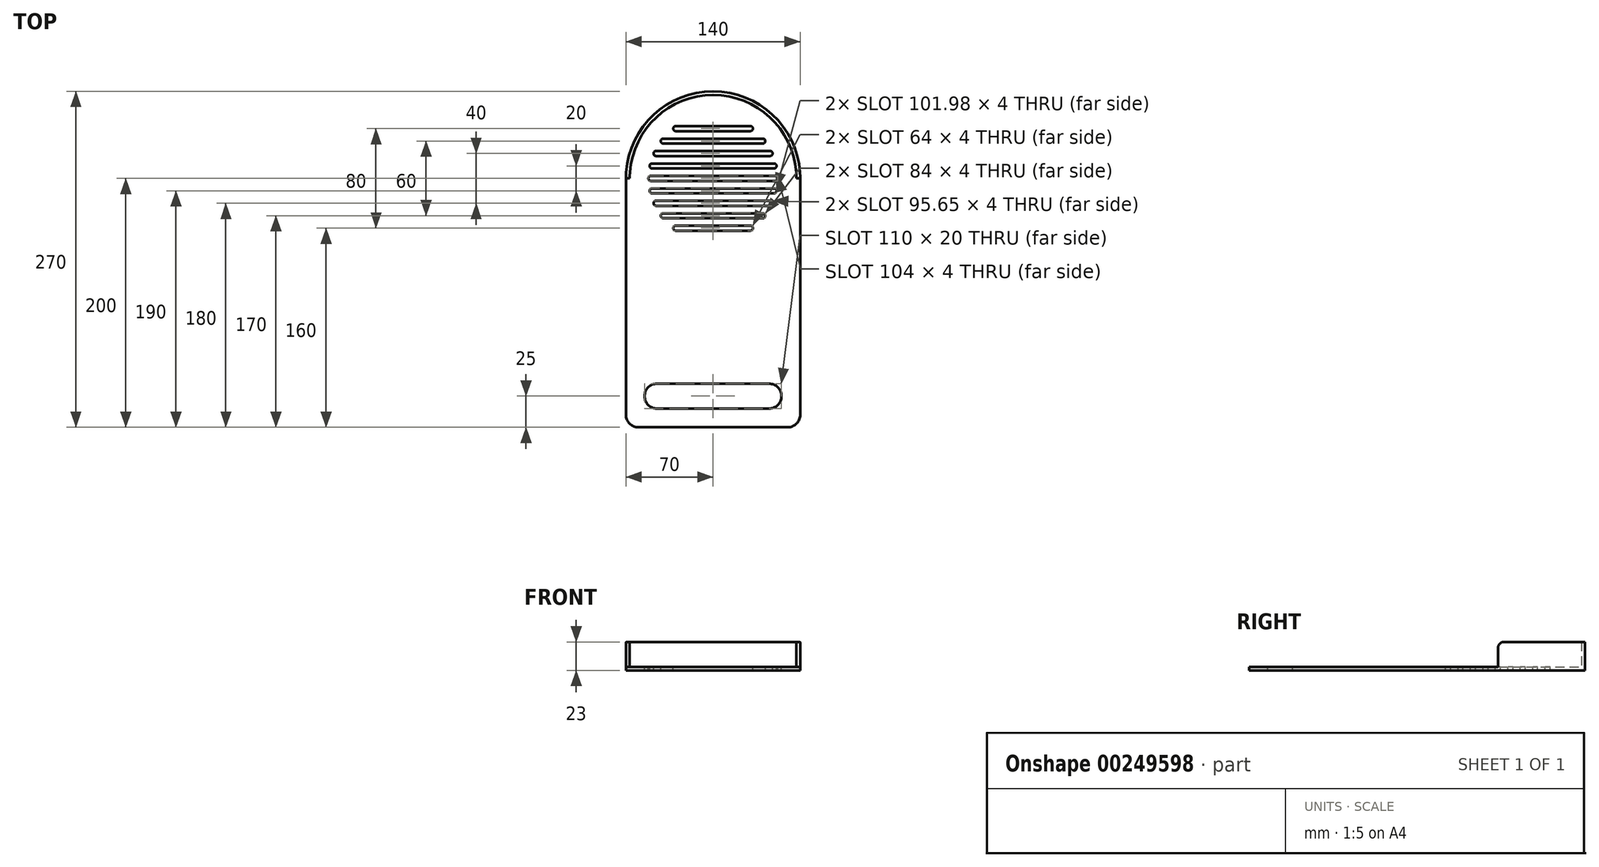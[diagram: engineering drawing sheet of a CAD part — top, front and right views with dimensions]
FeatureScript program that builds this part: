
annotation { "Feature Type Name" : "Feature", "Feature Type Description" : "" }
export const myFeature = defineFeature(function(context is Context, id is Id, definition is map)
    precondition{}
    {
        {
            var Q0;
            Q0=qCreatedBy(makeId("Top.planeOp"),FACE);
            var sketch = newSketch(context, id + "F0", { "sketchPlane" : qUnion([Q0])});
            skArc(sketch, "E0", {"start": v(70, 0) * mm, "mid": v(0, 70) * mm, "end": v(-70, 0) * mm});
            skLineSegment(sketch, "E1.top", {"start": v(-60, -200) * mm, "end": v(60, -200) * mm});
            skLineSegment(sketch, "E1.left", {"start": v(-70, 0) * mm, "end": v(-70, -190) * mm});
            skLineSegment(sketch, "E1.right", {"start": v(70, 0) * mm, "end": v(70, -190) * mm});
            skPoint(sketch, "E2.visualSharp", {"position": v(-70, -200) * mm});
            skArc(sketch, "E2.filletArc", {"start": v(-70, -190) * mm, "mid": v(-67.07, -197.07) * mm, "end": v(-60, -200) * mm});
            skPoint(sketch, "E3.visualSharp", {"position": v(70, -200) * mm});
            skArc(sketch, "E3.filletArc", {"start": v(60, -200) * mm, "mid": v(67.07, -197.07) * mm, "end": v(70, -190) * mm});
            skArc(sketch, "E4.0", {"start": v(67, 0) * mm, "mid": v(0, 67) * mm, "end": v(-67, 0) * mm});
            skLineSegment(sketch, "E5", {"start": v(-67, 0) * mm, "end": v(-70, 0) * mm});
            skLineSegment(sketch, "E6", {"start": v(67, 0) * mm, "end": v(70, 0) * mm});
            skLineSegment(sketch, "E7", {"start": v(-50, 0) * mm, "end": v(50, 0) * mm});
            skLineSegment(sketch, "E8", {"start": v(-48.99, 10) * mm, "end": v(48.99, 10) * mm});
            skLineSegment(sketch, "E9", {"start": v(-45.83, 20) * mm, "end": v(45.83, 20) * mm});
            skLineSegment(sketch, "E10", {"start": v(-40, 30) * mm, "end": v(40, 30) * mm});
            skLineSegment(sketch, "E11", {"start": v(-30, 40) * mm, "end": v(30, 40) * mm});
            skArc(sketch, "E12.0", {"start": v(50, 0) * mm, "mid": v(0, 50) * mm, "end": v(-50, 0) * mm, "construction": true});
            skArc(sketch, "E13.0.startCap", {"start": v(-50, -2) * mm, "mid": v(-52, 0) * mm, "end": v(-50, 2) * mm});
            skArc(sketch, "E13.0.endCap", {"start": v(50, 2) * mm, "mid": v(52, 0) * mm, "end": v(50, -2) * mm});
            skLineSegment(sketch, "E13.0.left", {"start": v(-50, 2) * mm, "end": v(50, 2) * mm});
            skLineSegment(sketch, "E13.0.right", {"start": v(-50, -2) * mm, "end": v(50, -2) * mm});
            skArc(sketch, "E14.0.startCap", {"start": v(-48.99, 8) * mm, "mid": v(-50.99, 10) * mm, "end": v(-48.99, 12) * mm});
            skArc(sketch, "E14.0.endCap", {"start": v(48.99, 12) * mm, "mid": v(50.99, 10) * mm, "end": v(48.99, 8) * mm});
            skLineSegment(sketch, "E14.0.left", {"start": v(-48.99, 12) * mm, "end": v(48.99, 12) * mm});
            skLineSegment(sketch, "E14.0.right", {"start": v(-48.99, 8) * mm, "end": v(48.99, 8) * mm});
            skArc(sketch, "E14.1.startCap", {"start": v(-45.83, 18) * mm, "mid": v(-47.83, 20) * mm, "end": v(-45.83, 22) * mm});
            skArc(sketch, "E14.1.endCap", {"start": v(45.83, 22) * mm, "mid": v(47.83, 20) * mm, "end": v(45.83, 18) * mm});
            skLineSegment(sketch, "E14.1.left", {"start": v(-45.83, 22) * mm, "end": v(45.83, 22) * mm});
            skLineSegment(sketch, "E14.1.right", {"start": v(-45.83, 18) * mm, "end": v(45.83, 18) * mm});
            skArc(sketch, "E14.2.startCap", {"start": v(-40, 28) * mm, "mid": v(-42, 30) * mm, "end": v(-40, 32) * mm});
            skArc(sketch, "E14.2.endCap", {"start": v(40, 32) * mm, "mid": v(42, 30) * mm, "end": v(40, 28) * mm});
            skLineSegment(sketch, "E14.2.left", {"start": v(-40, 32) * mm, "end": v(40, 32) * mm});
            skLineSegment(sketch, "E14.2.right", {"start": v(-40, 28) * mm, "end": v(40, 28) * mm});
            skArc(sketch, "E14.3.startCap", {"start": v(-30, 38) * mm, "mid": v(-32, 40) * mm, "end": v(-30, 42) * mm});
            skArc(sketch, "E14.3.endCap", {"start": v(30, 42) * mm, "mid": v(32, 40) * mm, "end": v(30, 38) * mm});
            skLineSegment(sketch, "E14.3.left", {"start": v(-30, 42) * mm, "end": v(30, 42) * mm});
            skLineSegment(sketch, "E14.3.right", {"start": v(-30, 38) * mm, "end": v(30, 38) * mm});
            skArc(sketch, "E15.MirrorCS", {"start": v(-48.99, -8) * mm, "mid": v(-50.99, -10) * mm, "end": v(-48.99, -12) * mm});
            skLineSegment(sketch, "E16.MirrorCS", {"start": v(-48.99, -12) * mm, "end": v(48.99, -12) * mm});
            skLineSegment(sketch, "E17.MirrorCS", {"start": v(-48.99, -8) * mm, "end": v(48.99, -8) * mm});
            skArc(sketch, "E18.MirrorCS", {"start": v(48.99, -12) * mm, "mid": v(50.99, -10) * mm, "end": v(48.99, -8) * mm});
            skArc(sketch, "E19.MirrorCS", {"start": v(30, -42) * mm, "mid": v(32, -40) * mm, "end": v(30, -38) * mm});
            skLineSegment(sketch, "E20.MirrorCS", {"start": v(-30, -42) * mm, "end": v(30, -42) * mm});
            skLineSegment(sketch, "E21.MirrorCS", {"start": v(-30, -38) * mm, "end": v(30, -38) * mm});
            skArc(sketch, "E22.MirrorCS", {"start": v(-30, -38) * mm, "mid": v(-32, -40) * mm, "end": v(-30, -42) * mm});
            skArc(sketch, "E23.MirrorCS", {"start": v(-40, -28) * mm, "mid": v(-42, -30) * mm, "end": v(-40, -32) * mm});
            skLineSegment(sketch, "E24.MirrorCS", {"start": v(-40, -32) * mm, "end": v(40, -32) * mm});
            skLineSegment(sketch, "E25.MirrorCS", {"start": v(-40, -28) * mm, "end": v(40, -28) * mm});
            skArc(sketch, "E26.MirrorCS", {"start": v(40, -32) * mm, "mid": v(42, -30) * mm, "end": v(40, -28) * mm});
            skArc(sketch, "E27.MirrorCS", {"start": v(45.83, -22) * mm, "mid": v(47.83, -20) * mm, "end": v(45.83, -18) * mm});
            skLineSegment(sketch, "E28.MirrorCS", {"start": v(-45.83, -22) * mm, "end": v(45.83, -22) * mm});
            skLineSegment(sketch, "E29.MirrorCS", {"start": v(-45.83, -18) * mm, "end": v(45.83, -18) * mm});
            skArc(sketch, "E30.MirrorCS", {"start": v(-45.83, -18) * mm, "mid": v(-47.83, -20) * mm, "end": v(-45.83, -22) * mm});
            skLineSegment(sketch, "E31", {"start": v(-45, -175) * mm, "end": v(45, -175) * mm});
            skLineSegment(sketch, "E32", {"start": v(0, -70) * mm, "end": v(0, -200) * mm, "construction": true});
            skPoint(sketch, "E33", {"position": v(0, -175) * mm});
            skArc(sketch, "E34.0.startCap", {"start": v(-45, -185) * mm, "mid": v(-55, -175) * mm, "end": v(-45, -165) * mm});
            skArc(sketch, "E34.0.endCap", {"start": v(45, -165) * mm, "mid": v(55, -175) * mm, "end": v(45, -185) * mm});
            skLineSegment(sketch, "E34.0.left", {"start": v(-45, -165) * mm, "end": v(45, -165) * mm});
            skLineSegment(sketch, "E34.0.right", {"start": v(-45, -185) * mm, "end": v(45, -185) * mm});
            skSolve(sketch);
        }
        {
            var Q0;
            Q0=makeQuery(id+"F0.imprint","IMPRINT",FACE,{"disambiguationData":[TD([[makeQuery(id+"F0.imprint","IMPRINT",EDGE,{"derivedFrom":sQuery(id+"F0.wireOp",EDGE,"E1.top")}),1.0]])]});
            var Q1;
            Q1=makeQuery(id+"F0.imprint","IMPRINT",FACE,{"disambiguationData":[TD([[makeQuery(id+"F0.imprint","IMPRINT",EDGE,{"derivedFrom":sQuery(id+"F0.wireOp",EDGE,"E0")}),1.0]])]});
            extrude(context, id + "F1", {"entities" : qUnion([Q0, Q1]), "oppositeDirection" : true, "depth" : 3 * mm});
        }
        {
            var Q0;
            Q0=makeQuery(id+"F0.imprint","IMPRINT",FACE,{"disambiguationData":[TD([[makeQuery(id+"F0.imprint","IMPRINT",EDGE,{"derivedFrom":sQuery(id+"F0.wireOp",EDGE,"E0")}),1.0]])]});
            extrude(context, id + "F2", {"entities" : qUnion([Q0]), "operationType" : NewBodyOperationType.ADD, "depth" : 20 * mm});
        }
        {
            var Q0;
            Q0=makeQuery(id+"F2.opExtrude","CAP_EDGE",EDGE,{"disambiguationData":[OSD([sQuery(id+"F0.wireOp",EDGE,"E5")])],"isStart":false});
            var Q1;
            Q1=makeQuery(id+"F2.opExtrude","CAP_EDGE",EDGE,{"disambiguationData":[OSD([sQuery(id+"F0.wireOp",EDGE,"E6")])],"isStart":false});
            fillet(context, id + "F3", {"entities" : qUnion([Q0, Q1]), "radius" : 5 * mm, "tangentPropagation" : true, "allowEdgeOverflow" : false});
        }
    });
